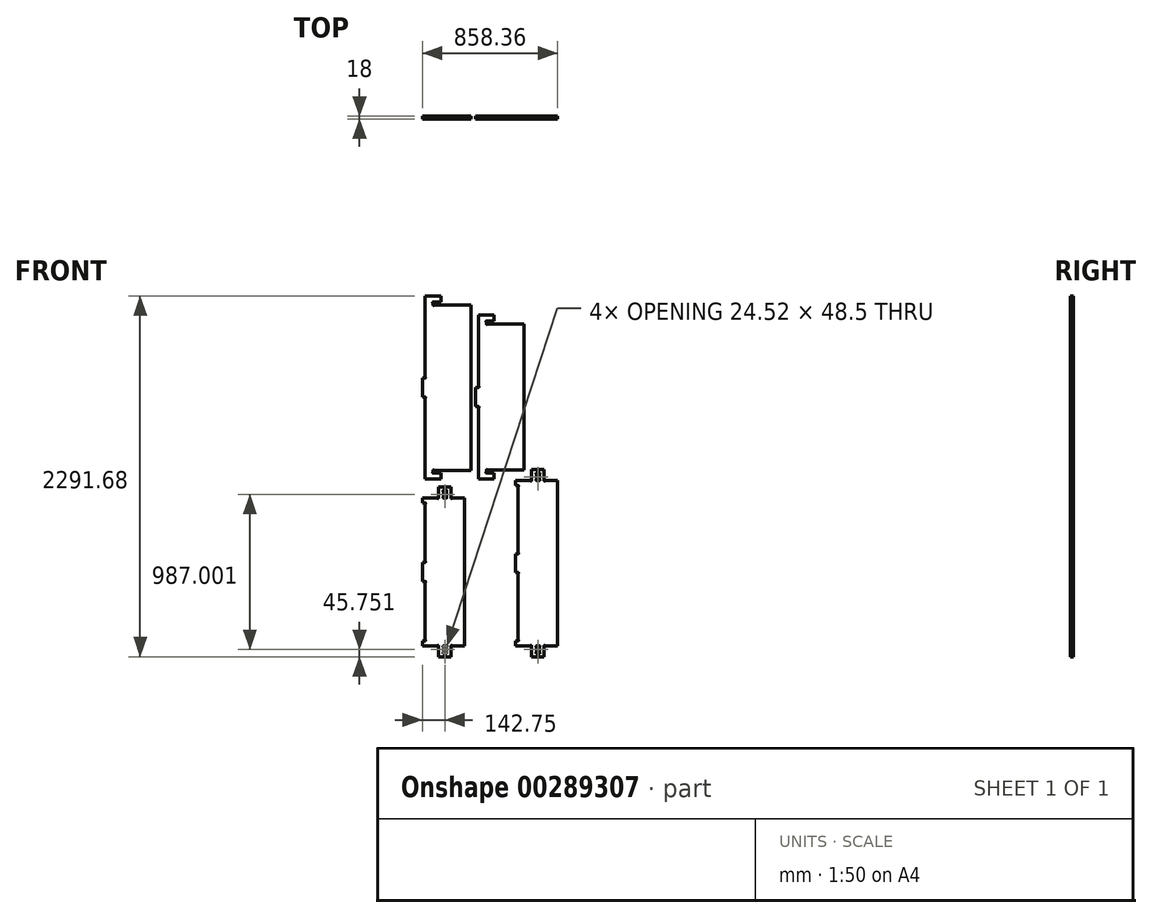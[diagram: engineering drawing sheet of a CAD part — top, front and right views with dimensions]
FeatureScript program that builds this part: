
annotation { "Feature Type Name" : "Feature", "Feature Type Description" : "" }
export const myFeature = defineFeature(function(context is Context, id is Id, definition is map)
    precondition{}
    {
        {
            var Q0;
            Q0=qCreatedBy(makeId("Front.planeOp"),FACE);
            var sketch = newSketch(context, id + "F0", { "sketchPlane" : qUnion([Q0])});
            skLineSegment(sketch, "E0", {"start": v(-600, -1200) * mm, "end": v(600, -1200) * mm});
            skLineSegment(sketch, "E1", {"start": v(600, -1200) * mm, "end": v(600, 1200) * mm});
            skLineSegment(sketch, "E2", {"start": v(600, 1200) * mm, "end": v(-600, 1200) * mm});
            skLineSegment(sketch, "E3", {"start": v(-600, 1200) * mm, "end": v(-600, -1200) * mm});
            skLineSegment(sketch, "E4", {"start": v(-266.04, 1059.68) * mm, "end": v(-501.48, 1059.68) * mm});
            skArc(sketch, "E5", {"start": v(-501.48, 1059.68) * mm, "mid": v(-504.49, 1056.67) * mm, "end": v(-507.5, 1059.68) * mm});
            skLineSegment(sketch, "E6", {"start": v(-507.5, 1059.68) * mm, "end": v(-507.5, 1072.16) * mm});
            skArc(sketch, "E7", {"start": v(-507.5, 1072.16) * mm, "mid": v(-510.5, 1075.17) * mm, "end": v(-507.5, 1078.18) * mm});
            skLineSegment(sketch, "E8", {"start": v(-507.5, 1078.18) * mm, "end": v(-457.5, 1078.18) * mm});
            skLineSegment(sketch, "E9", {"start": v(-457.5, 1078.18) * mm, "end": v(-457.5, 1116.68) * mm});
            skLineSegment(sketch, "E10", {"start": v(-457.5, 1116.68) * mm, "end": v(-557, 1116.68) * mm});
            skLineSegment(sketch, "E11", {"start": v(-557, 1116.68) * mm, "end": v(-557, 600.7) * mm});
            skArc(sketch, "E12", {"start": v(-557, 600.7) * mm, "mid": v(-553.99, 597.69) * mm, "end": v(-557, 594.68) * mm});
            skLineSegment(sketch, "E13", {"start": v(-557, 594.68) * mm, "end": v(-575, 594.68) * mm});
            skLineSegment(sketch, "E14", {"start": v(-575, 594.68) * mm, "end": v(-575, 475.18) * mm});
            skLineSegment(sketch, "E15", {"start": v(-575, 475.18) * mm, "end": v(-557, 475.18) * mm});
            skArc(sketch, "E16", {"start": v(-557, 475.18) * mm, "mid": v(-553.99, 472.17) * mm, "end": v(-557, 469.16) * mm});
            skLineSegment(sketch, "E17", {"start": v(-557, 469.16) * mm, "end": v(-557, -46.82) * mm});
            skLineSegment(sketch, "E18", {"start": v(-557, -46.82) * mm, "end": v(-457.5, -46.82) * mm});
            skLineSegment(sketch, "E19", {"start": v(-457.5, -46.82) * mm, "end": v(-457.5, -8.32) * mm});
            skLineSegment(sketch, "E20", {"start": v(-457.5, -8.32) * mm, "end": v(-507.5, -8.32) * mm});
            skArc(sketch, "E21", {"start": v(-507.5, -8.32) * mm, "mid": v(-510.5, -5.31) * mm, "end": v(-507.5, -2.3) * mm});
            skLineSegment(sketch, "E22", {"start": v(-507.5, -2.3) * mm, "end": v(-507.5, 10.18) * mm});
            skArc(sketch, "E23", {"start": v(-507.5, 10.18) * mm, "mid": v(-504.49, 13.19) * mm, "end": v(-501.48, 10.18) * mm});
            skLineSegment(sketch, "E24", {"start": v(-501.48, 10.18) * mm, "end": v(-266.04, 10.18) * mm});
            skLineSegment(sketch, "E25", {"start": v(-266.04, 10.18) * mm, "end": v(-266.04, 1059.68) * mm});
            skLineSegment(sketch, "E26", {"start": v(-168.7, -1.99) * mm, "end": v(-168.7, 10.5) * mm});
            skArc(sketch, "E27", {"start": v(-168.7, 10.5) * mm, "mid": v(-165.7, 13.5) * mm, "end": v(-162.68, 10.5) * mm});
            skLineSegment(sketch, "E28", {"start": v(-162.68, 10.5) * mm, "end": v(69.97, 10.5) * mm});
            skLineSegment(sketch, "E29", {"start": v(69.97, 10.5) * mm, "end": v(69.97, 940) * mm});
            skLineSegment(sketch, "E30", {"start": v(69.97, 940) * mm, "end": v(-162.68, 940) * mm});
            skArc(sketch, "E31", {"start": v(-162.68, 940) * mm, "mid": v(-165.7, 936.98) * mm, "end": v(-168.7, 940) * mm});
            skLineSegment(sketch, "E32", {"start": v(-168.7, 940) * mm, "end": v(-168.7, 952.47) * mm});
            skArc(sketch, "E33", {"start": v(-168.7, 952.47) * mm, "mid": v(-171.71, 955.48) * mm, "end": v(-168.7, 958.5) * mm});
            skLineSegment(sketch, "E34", {"start": v(-168.7, 958.5) * mm, "end": v(-118.7, 958.5) * mm});
            skLineSegment(sketch, "E35", {"start": v(-118.7, 958.5) * mm, "end": v(-118.7, 997) * mm});
            skLineSegment(sketch, "E36", {"start": v(-118.7, 997) * mm, "end": v(-218.2, 997) * mm});
            skLineSegment(sketch, "E37", {"start": v(-218.2, 997) * mm, "end": v(-218.2, 541.01) * mm});
            skArc(sketch, "E38", {"start": v(-218.2, 541.01) * mm, "mid": v(-215.2, 538) * mm, "end": v(-218.2, 535) * mm});
            skLineSegment(sketch, "E39", {"start": v(-218.2, 535) * mm, "end": v(-236.2, 535) * mm});
            skLineSegment(sketch, "E40", {"start": v(-236.2, 535) * mm, "end": v(-236.2, 415.5) * mm});
            skLineSegment(sketch, "E41", {"start": v(-236.2, 415.5) * mm, "end": v(-218.2, 415.5) * mm});
            skArc(sketch, "E42", {"start": v(-218.2, 415.5) * mm, "mid": v(-215.2, 412.48) * mm, "end": v(-218.2, 409.47) * mm});
            skLineSegment(sketch, "E43", {"start": v(-218.2, 409.47) * mm, "end": v(-218.2, -46.5) * mm});
            skLineSegment(sketch, "E44", {"start": v(-218.2, -46.5) * mm, "end": v(-118.7, -46.5) * mm});
            skLineSegment(sketch, "E45", {"start": v(-118.7, -46.5) * mm, "end": v(-118.7, -8) * mm});
            skLineSegment(sketch, "E46", {"start": v(-118.7, -8) * mm, "end": v(-168.7, -8) * mm});
            skArc(sketch, "E47", {"start": v(-168.7, -8) * mm, "mid": v(-171.71, -5) * mm, "end": v(-168.7, -1.99) * mm});
            skLineSegment(sketch, "E48", {"start": v(575, -55.5) * mm, "end": v(496.02, -55.5) * mm});
            skArc(sketch, "E49", {"start": v(496.02, -55.5) * mm, "mid": v(493, -58.5) * mm, "end": v(490, -55.5) * mm});
            skLineSegment(sketch, "E50", {"start": v(490, -55.5) * mm, "end": v(490, 14.5) * mm});
            skLineSegment(sketch, "E51", {"start": v(490, 14.5) * mm, "end": v(410.5, 14.5) * mm});
            skLineSegment(sketch, "E52", {"start": v(410.5, 14.5) * mm, "end": v(410.5, -55.5) * mm});
            skArc(sketch, "E53", {"start": v(410.5, -55.5) * mm, "mid": v(407.49, -58.5) * mm, "end": v(404.48, -55.5) * mm});
            skLineSegment(sketch, "E54", {"start": v(404.48, -55.5) * mm, "end": v(307.5, -55.5) * mm});
            skLineSegment(sketch, "E55", {"start": v(307.5, -55.5) * mm, "end": v(307.5, -86) * mm});
            skLineSegment(sketch, "E56", {"start": v(307.5, -86) * mm, "end": v(325.5, -86) * mm});
            skArc(sketch, "E57", {"start": v(325.5, -86) * mm, "mid": v(328.5, -89) * mm, "end": v(325.5, -92.02) * mm});
            skLineSegment(sketch, "E58", {"start": v(325.5, -92.02) * mm, "end": v(325.5, -514.48) * mm});
            skArc(sketch, "E59", {"start": v(325.5, -514.48) * mm, "mid": v(328.5, -517.49) * mm, "end": v(325.5, -520.5) * mm});
            skLineSegment(sketch, "E60", {"start": v(325.5, -520.5) * mm, "end": v(307.5, -520.5) * mm});
            skLineSegment(sketch, "E61", {"start": v(307.5, -520.5) * mm, "end": v(307.5, -640) * mm});
            skLineSegment(sketch, "E62", {"start": v(307.5, -640) * mm, "end": v(325.5, -640) * mm});
            skArc(sketch, "E63", {"start": v(325.5, -640) * mm, "mid": v(328.5, -643) * mm, "end": v(325.5, -646.02) * mm});
            skLineSegment(sketch, "E64", {"start": v(325.5, -646.02) * mm, "end": v(325.5, -1068.48) * mm});
            skArc(sketch, "E65", {"start": v(325.5, -1068.48) * mm, "mid": v(328.5, -1071.49) * mm, "end": v(325.5, -1074.5) * mm});
            skLineSegment(sketch, "E66", {"start": v(325.5, -1074.5) * mm, "end": v(307.5, -1074.5) * mm});
            skLineSegment(sketch, "E67", {"start": v(307.5, -1074.5) * mm, "end": v(307.5, -1105) * mm});
            skLineSegment(sketch, "E68", {"start": v(307.5, -1105) * mm, "end": v(404.48, -1105) * mm});
            skArc(sketch, "E69", {"start": v(404.48, -1105) * mm, "mid": v(407.49, -1101.99) * mm, "end": v(410.5, -1105) * mm});
            skLineSegment(sketch, "E70", {"start": v(410.5, -1105) * mm, "end": v(410.5, -1175) * mm});
            skLineSegment(sketch, "E71", {"start": v(410.5, -1175) * mm, "end": v(490, -1175) * mm});
            skLineSegment(sketch, "E72", {"start": v(490, -1175) * mm, "end": v(490, -1105) * mm});
            skArc(sketch, "E73", {"start": v(490, -1105) * mm, "mid": v(493, -1101.99) * mm, "end": v(496.02, -1105) * mm});
            skLineSegment(sketch, "E74", {"start": v(496.02, -1105) * mm, "end": v(575, -1105) * mm});
            skLineSegment(sketch, "E75", {"start": v(575, -1105) * mm, "end": v(575, -55.5) * mm});
            skLineSegment(sketch, "E76", {"start": v(-15.96, -166.5) * mm, "end": v(-94.94, -166.5) * mm});
            skArc(sketch, "E77", {"start": v(-94.94, -166.5) * mm, "mid": v(-97.95, -169.5) * mm, "end": v(-100.96, -166.5) * mm});
            skLineSegment(sketch, "E78", {"start": v(-100.96, -166.5) * mm, "end": v(-100.96, -96.5) * mm});
            skLineSegment(sketch, "E79", {"start": v(-100.96, -96.5) * mm, "end": v(-180.46, -96.5) * mm});
            skLineSegment(sketch, "E80", {"start": v(-180.46, -96.5) * mm, "end": v(-180.46, -166.5) * mm});
            skArc(sketch, "E81", {"start": v(-180.46, -166.5) * mm, "mid": v(-183.47, -169.5) * mm, "end": v(-186.48, -166.5) * mm});
            skLineSegment(sketch, "E82", {"start": v(-186.48, -166.5) * mm, "end": v(-283.46, -166.5) * mm});
            skLineSegment(sketch, "E83", {"start": v(-283.46, -166.5) * mm, "end": v(-283.46, -197) * mm});
            skLineSegment(sketch, "E84", {"start": v(-283.46, -197) * mm, "end": v(-265.46, -197) * mm});
            skArc(sketch, "E85", {"start": v(-265.46, -197) * mm, "mid": v(-262.45, -200) * mm, "end": v(-265.46, -203.02) * mm});
            skLineSegment(sketch, "E86", {"start": v(-265.46, -203.02) * mm, "end": v(-265.46, -569.98) * mm});
            skArc(sketch, "E87", {"start": v(-265.46, -569.98) * mm, "mid": v(-262.45, -572.99) * mm, "end": v(-265.46, -576) * mm});
            skLineSegment(sketch, "E88", {"start": v(-265.46, -576) * mm, "end": v(-283.46, -576) * mm});
            skLineSegment(sketch, "E89", {"start": v(-283.46, -576) * mm, "end": v(-283.46, -695.5) * mm});
            skLineSegment(sketch, "E90", {"start": v(-283.46, -695.5) * mm, "end": v(-265.46, -695.5) * mm});
            skArc(sketch, "E91", {"start": v(-265.46, -695.5) * mm, "mid": v(-262.45, -698.5) * mm, "end": v(-265.46, -701.52) * mm});
            skLineSegment(sketch, "E92", {"start": v(-265.46, -701.52) * mm, "end": v(-265.46, -1068.48) * mm});
            skArc(sketch, "E93", {"start": v(-265.46, -1068.48) * mm, "mid": v(-262.45, -1071.49) * mm, "end": v(-265.46, -1074.5) * mm});
            skLineSegment(sketch, "E94", {"start": v(-265.46, -1074.5) * mm, "end": v(-283.46, -1074.5) * mm});
            skLineSegment(sketch, "E95", {"start": v(-283.46, -1074.5) * mm, "end": v(-283.46, -1105) * mm});
            skLineSegment(sketch, "E96", {"start": v(-283.46, -1105) * mm, "end": v(-186.48, -1105) * mm});
            skArc(sketch, "E97", {"start": v(-186.48, -1105) * mm, "mid": v(-183.47, -1101.99) * mm, "end": v(-180.46, -1105) * mm});
            skLineSegment(sketch, "E98", {"start": v(-180.46, -1105) * mm, "end": v(-180.46, -1175) * mm});
            skLineSegment(sketch, "E99", {"start": v(-180.46, -1175) * mm, "end": v(-100.96, -1175) * mm});
            skLineSegment(sketch, "E100", {"start": v(-100.96, -1175) * mm, "end": v(-100.96, -1105) * mm});
            skArc(sketch, "E101", {"start": v(-100.96, -1105) * mm, "mid": v(-97.95, -1101.99) * mm, "end": v(-94.94, -1105) * mm});
            skLineSegment(sketch, "E102", {"start": v(-94.94, -1105) * mm, "end": v(-15.96, -1105) * mm});
            skLineSegment(sketch, "E103", {"start": v(-15.96, -1105) * mm, "end": v(-15.96, -166.5) * mm});
            skLineSegment(sketch, "E104", {"start": v(-307.5, -166.5) * mm, "end": v(-386.48, -166.5) * mm});
            skArc(sketch, "E105", {"start": v(-386.48, -166.5) * mm, "mid": v(-389.49, -169.5) * mm, "end": v(-392.5, -166.5) * mm});
            skLineSegment(sketch, "E106", {"start": v(-392.5, -166.5) * mm, "end": v(-392.5, -96.5) * mm});
            skLineSegment(sketch, "E107", {"start": v(-392.5, -96.5) * mm, "end": v(-472, -96.5) * mm});
            skLineSegment(sketch, "E108", {"start": v(-472, -96.5) * mm, "end": v(-472, -166.5) * mm});
            skArc(sketch, "E109", {"start": v(-472, -166.5) * mm, "mid": v(-475, -169.5) * mm, "end": v(-478.02, -166.5) * mm});
            skLineSegment(sketch, "E110", {"start": v(-478.02, -166.5) * mm, "end": v(-575, -166.5) * mm});
            skLineSegment(sketch, "E111", {"start": v(-575, -166.5) * mm, "end": v(-575, -197) * mm});
            skLineSegment(sketch, "E112", {"start": v(-575, -197) * mm, "end": v(-557, -197) * mm});
            skArc(sketch, "E113", {"start": v(-557, -197) * mm, "mid": v(-553.99, -200) * mm, "end": v(-557, -203.02) * mm});
            skLineSegment(sketch, "E114", {"start": v(-557, -203.02) * mm, "end": v(-557, -569.98) * mm});
            skArc(sketch, "E115", {"start": v(-557, -569.98) * mm, "mid": v(-553.99, -572.99) * mm, "end": v(-557, -576) * mm});
            skLineSegment(sketch, "E116", {"start": v(-557, -576) * mm, "end": v(-575, -576) * mm});
            skLineSegment(sketch, "E117", {"start": v(-575, -576) * mm, "end": v(-575, -695.5) * mm});
            skLineSegment(sketch, "E118", {"start": v(-575, -695.5) * mm, "end": v(-557, -695.5) * mm});
            skArc(sketch, "E119", {"start": v(-557, -695.5) * mm, "mid": v(-553.99, -698.5) * mm, "end": v(-557, -701.52) * mm});
            skLineSegment(sketch, "E120", {"start": v(-557, -701.52) * mm, "end": v(-557, -1068.48) * mm});
            skArc(sketch, "E121", {"start": v(-557, -1068.48) * mm, "mid": v(-553.99, -1071.49) * mm, "end": v(-557, -1074.5) * mm});
            skLineSegment(sketch, "E122", {"start": v(-557, -1074.5) * mm, "end": v(-575, -1074.5) * mm});
            skLineSegment(sketch, "E123", {"start": v(-575, -1074.5) * mm, "end": v(-575, -1105) * mm});
            skLineSegment(sketch, "E124", {"start": v(-575, -1105) * mm, "end": v(-478.02, -1105) * mm});
            skArc(sketch, "E125", {"start": v(-478.02, -1105) * mm, "mid": v(-475, -1101.99) * mm, "end": v(-472, -1105) * mm});
            skLineSegment(sketch, "E126", {"start": v(-472, -1105) * mm, "end": v(-472, -1175) * mm});
            skLineSegment(sketch, "E127", {"start": v(-472, -1175) * mm, "end": v(-392.5, -1175) * mm});
            skLineSegment(sketch, "E128", {"start": v(-392.5, -1175) * mm, "end": v(-392.5, -1105) * mm});
            skArc(sketch, "E129", {"start": v(-392.5, -1105) * mm, "mid": v(-389.49, -1101.99) * mm, "end": v(-386.48, -1105) * mm});
            skLineSegment(sketch, "E130", {"start": v(-386.48, -1105) * mm, "end": v(-307.5, -1105) * mm});
            skLineSegment(sketch, "E131", {"start": v(-307.5, -1105) * mm, "end": v(-307.5, -166.5) * mm});
            skLineSegment(sketch, "E132", {"start": v(283.36, -55.5) * mm, "end": v(204.38, -55.5) * mm});
            skArc(sketch, "E133", {"start": v(204.38, -55.5) * mm, "mid": v(201.37, -58.5) * mm, "end": v(198.36, -55.5) * mm});
            skLineSegment(sketch, "E134", {"start": v(198.36, -55.5) * mm, "end": v(198.36, 14.5) * mm});
            skLineSegment(sketch, "E135", {"start": v(198.36, 14.5) * mm, "end": v(118.86, 14.5) * mm});
            skLineSegment(sketch, "E136", {"start": v(118.86, 14.5) * mm, "end": v(118.86, -55.5) * mm});
            skArc(sketch, "E137", {"start": v(118.86, -55.5) * mm, "mid": v(115.85, -58.5) * mm, "end": v(112.84, -55.5) * mm});
            skLineSegment(sketch, "E138", {"start": v(112.84, -55.5) * mm, "end": v(15.86, -55.5) * mm});
            skLineSegment(sketch, "E139", {"start": v(15.86, -55.5) * mm, "end": v(15.86, -86) * mm});
            skLineSegment(sketch, "E140", {"start": v(15.86, -86) * mm, "end": v(33.86, -86) * mm});
            skArc(sketch, "E141", {"start": v(33.86, -86) * mm, "mid": v(36.87, -89) * mm, "end": v(33.86, -92.02) * mm});
            skLineSegment(sketch, "E142", {"start": v(33.86, -92.02) * mm, "end": v(33.86, -514.48) * mm});
            skArc(sketch, "E143", {"start": v(33.86, -514.48) * mm, "mid": v(36.87, -517.49) * mm, "end": v(33.86, -520.5) * mm});
            skLineSegment(sketch, "E144", {"start": v(33.86, -520.5) * mm, "end": v(15.86, -520.5) * mm});
            skLineSegment(sketch, "E145", {"start": v(15.86, -520.5) * mm, "end": v(15.86, -640) * mm});
            skLineSegment(sketch, "E146", {"start": v(15.86, -640) * mm, "end": v(33.86, -640) * mm});
            skArc(sketch, "E147", {"start": v(33.86, -640) * mm, "mid": v(36.87, -643) * mm, "end": v(33.86, -646.02) * mm});
            skLineSegment(sketch, "E148", {"start": v(33.86, -646.02) * mm, "end": v(33.86, -1068.48) * mm});
            skArc(sketch, "E149", {"start": v(33.86, -1068.48) * mm, "mid": v(36.87, -1071.49) * mm, "end": v(33.86, -1074.5) * mm});
            skLineSegment(sketch, "E150", {"start": v(33.86, -1074.5) * mm, "end": v(15.86, -1074.5) * mm});
            skLineSegment(sketch, "E151", {"start": v(15.86, -1074.5) * mm, "end": v(15.86, -1105) * mm});
            skLineSegment(sketch, "E152", {"start": v(15.86, -1105) * mm, "end": v(112.84, -1105) * mm});
            skArc(sketch, "E153", {"start": v(112.84, -1105) * mm, "mid": v(115.85, -1101.99) * mm, "end": v(118.86, -1105) * mm});
            skLineSegment(sketch, "E154", {"start": v(118.86, -1105) * mm, "end": v(118.86, -1175) * mm});
            skLineSegment(sketch, "E155", {"start": v(118.86, -1175) * mm, "end": v(198.36, -1175) * mm});
            skLineSegment(sketch, "E156", {"start": v(198.36, -1175) * mm, "end": v(198.36, -1105) * mm});
            skArc(sketch, "E157", {"start": v(198.36, -1105) * mm, "mid": v(201.37, -1101.99) * mm, "end": v(204.38, -1105) * mm});
            skLineSegment(sketch, "E158", {"start": v(204.38, -1105) * mm, "end": v(283.36, -1105) * mm});
            skLineSegment(sketch, "E159", {"start": v(283.36, -1105) * mm, "end": v(283.36, -55.5) * mm});
            skLineSegment(sketch, "E160", {"start": v(459.5, -1147.48) * mm, "end": v(459.5, -1111.02) * mm});
            skArc(sketch, "E161", {"start": v(459.5, -1111.02) * mm, "mid": v(462.5, -1108) * mm, "end": v(459.5, -1105) * mm});
            skLineSegment(sketch, "E162", {"start": v(459.5, -1105) * mm, "end": v(441, -1105) * mm});
            skArc(sketch, "E163", {"start": v(441, -1105) * mm, "mid": v(437.99, -1108) * mm, "end": v(441, -1111.02) * mm});
            skLineSegment(sketch, "E164", {"start": v(441, -1111.02) * mm, "end": v(441, -1147.48) * mm});
            skArc(sketch, "E165", {"start": v(441, -1147.48) * mm, "mid": v(437.99, -1150.49) * mm, "end": v(441, -1153.5) * mm});
            skLineSegment(sketch, "E166", {"start": v(441, -1153.5) * mm, "end": v(459.5, -1153.5) * mm});
            skArc(sketch, "E167", {"start": v(459.5, -1153.5) * mm, "mid": v(462.5, -1150.49) * mm, "end": v(459.5, -1147.48) * mm});
            skLineSegment(sketch, "E168", {"start": v(459.5, -49.48) * mm, "end": v(459.5, -13.02) * mm});
            skArc(sketch, "E169", {"start": v(459.5, -13.02) * mm, "mid": v(462.5, -10) * mm, "end": v(459.5, -7) * mm});
            skLineSegment(sketch, "E170", {"start": v(459.5, -7) * mm, "end": v(441, -7) * mm});
            skArc(sketch, "E171", {"start": v(441, -7) * mm, "mid": v(437.99, -10) * mm, "end": v(441, -13.02) * mm});
            skLineSegment(sketch, "E172", {"start": v(441, -13.02) * mm, "end": v(441, -49.48) * mm});
            skArc(sketch, "E173", {"start": v(441, -49.48) * mm, "mid": v(437.99, -52.49) * mm, "end": v(441, -55.5) * mm});
            skLineSegment(sketch, "E174", {"start": v(441, -55.5) * mm, "end": v(459.5, -55.5) * mm});
            skArc(sketch, "E175", {"start": v(459.5, -55.5) * mm, "mid": v(462.5, -52.49) * mm, "end": v(459.5, -49.48) * mm});
            skLineSegment(sketch, "E176", {"start": v(-131.46, -1147.48) * mm, "end": v(-131.46, -1111.02) * mm});
            skArc(sketch, "E177", {"start": v(-131.46, -1111.02) * mm, "mid": v(-128.45, -1108) * mm, "end": v(-131.46, -1105) * mm});
            skLineSegment(sketch, "E178", {"start": v(-131.46, -1105) * mm, "end": v(-149.96, -1105) * mm});
            skArc(sketch, "E179", {"start": v(-149.96, -1105) * mm, "mid": v(-152.97, -1108) * mm, "end": v(-149.96, -1111.02) * mm});
            skLineSegment(sketch, "E180", {"start": v(-149.96, -1111.02) * mm, "end": v(-149.96, -1147.48) * mm});
            skArc(sketch, "E181", {"start": v(-149.96, -1147.48) * mm, "mid": v(-152.97, -1150.49) * mm, "end": v(-149.96, -1153.5) * mm});
            skLineSegment(sketch, "E182", {"start": v(-149.96, -1153.5) * mm, "end": v(-131.46, -1153.5) * mm});
            skArc(sketch, "E183", {"start": v(-131.46, -1153.5) * mm, "mid": v(-128.45, -1150.49) * mm, "end": v(-131.46, -1147.48) * mm});
            skLineSegment(sketch, "E184", {"start": v(-149.96, -124.02) * mm, "end": v(-149.96, -160.48) * mm});
            skArc(sketch, "E185", {"start": v(-149.96, -160.48) * mm, "mid": v(-152.97, -163.49) * mm, "end": v(-149.96, -166.5) * mm});
            skLineSegment(sketch, "E186", {"start": v(-149.96, -166.5) * mm, "end": v(-131.46, -166.5) * mm});
            skArc(sketch, "E187", {"start": v(-131.46, -166.5) * mm, "mid": v(-128.45, -163.49) * mm, "end": v(-131.46, -160.48) * mm});
            skLineSegment(sketch, "E188", {"start": v(-131.46, -160.48) * mm, "end": v(-131.46, -124.02) * mm});
            skArc(sketch, "E189", {"start": v(-131.46, -124.02) * mm, "mid": v(-128.45, -121) * mm, "end": v(-131.46, -118) * mm});
            skLineSegment(sketch, "E190", {"start": v(-131.46, -118) * mm, "end": v(-149.96, -118) * mm});
            skArc(sketch, "E191", {"start": v(-149.96, -118) * mm, "mid": v(-152.97, -121) * mm, "end": v(-149.96, -124.02) * mm});
            skLineSegment(sketch, "E192", {"start": v(-423, -1147.48) * mm, "end": v(-423, -1111.02) * mm});
            skArc(sketch, "E193", {"start": v(-423, -1111.02) * mm, "mid": v(-419.99, -1108) * mm, "end": v(-423, -1105) * mm});
            skLineSegment(sketch, "E194", {"start": v(-423, -1105) * mm, "end": v(-441.5, -1105) * mm});
            skArc(sketch, "E195", {"start": v(-441.5, -1105) * mm, "mid": v(-444.5, -1108) * mm, "end": v(-441.5, -1111.02) * mm});
            skLineSegment(sketch, "E196", {"start": v(-441.5, -1111.02) * mm, "end": v(-441.5, -1147.48) * mm});
            skArc(sketch, "E197", {"start": v(-441.5, -1147.48) * mm, "mid": v(-444.5, -1150.49) * mm, "end": v(-441.5, -1153.5) * mm});
            skLineSegment(sketch, "E198", {"start": v(-441.5, -1153.5) * mm, "end": v(-423, -1153.5) * mm});
            skArc(sketch, "E199", {"start": v(-423, -1153.5) * mm, "mid": v(-419.99, -1150.49) * mm, "end": v(-423, -1147.48) * mm});
            skLineSegment(sketch, "E200", {"start": v(-441.5, -124.02) * mm, "end": v(-441.5, -160.48) * mm});
            skArc(sketch, "E201", {"start": v(-441.5, -160.48) * mm, "mid": v(-444.5, -163.49) * mm, "end": v(-441.5, -166.5) * mm});
            skLineSegment(sketch, "E202", {"start": v(-441.5, -166.5) * mm, "end": v(-423, -166.5) * mm});
            skArc(sketch, "E203", {"start": v(-423, -166.5) * mm, "mid": v(-419.99, -163.49) * mm, "end": v(-423, -160.48) * mm});
            skLineSegment(sketch, "E204", {"start": v(-423, -160.48) * mm, "end": v(-423, -124.02) * mm});
            skArc(sketch, "E205", {"start": v(-423, -124.02) * mm, "mid": v(-419.99, -121) * mm, "end": v(-423, -118) * mm});
            skLineSegment(sketch, "E206", {"start": v(-423, -118) * mm, "end": v(-441.5, -118) * mm});
            skArc(sketch, "E207", {"start": v(-441.5, -118) * mm, "mid": v(-444.5, -121) * mm, "end": v(-441.5, -124.02) * mm});
            skLineSegment(sketch, "E208", {"start": v(167.86, -1147.48) * mm, "end": v(167.86, -1111.02) * mm});
            skArc(sketch, "E209", {"start": v(167.86, -1111.02) * mm, "mid": v(170.87, -1108) * mm, "end": v(167.86, -1105) * mm});
            skLineSegment(sketch, "E210", {"start": v(167.86, -1105) * mm, "end": v(149.36, -1105) * mm});
            skArc(sketch, "E211", {"start": v(149.36, -1105) * mm, "mid": v(146.35, -1108) * mm, "end": v(149.36, -1111.02) * mm});
            skLineSegment(sketch, "E212", {"start": v(149.36, -1111.02) * mm, "end": v(149.36, -1147.48) * mm});
            skArc(sketch, "E213", {"start": v(149.36, -1147.48) * mm, "mid": v(146.35, -1150.49) * mm, "end": v(149.36, -1153.5) * mm});
            skLineSegment(sketch, "E214", {"start": v(149.36, -1153.5) * mm, "end": v(167.86, -1153.5) * mm});
            skArc(sketch, "E215", {"start": v(167.86, -1153.5) * mm, "mid": v(170.87, -1150.49) * mm, "end": v(167.86, -1147.48) * mm});
            skLineSegment(sketch, "E216", {"start": v(167.86, -49.48) * mm, "end": v(167.86, -13.02) * mm});
            skArc(sketch, "E217", {"start": v(167.86, -13.02) * mm, "mid": v(170.87, -10) * mm, "end": v(167.86, -7) * mm});
            skLineSegment(sketch, "E218", {"start": v(167.86, -7) * mm, "end": v(149.36, -7) * mm});
            skArc(sketch, "E219", {"start": v(149.36, -7) * mm, "mid": v(146.35, -10) * mm, "end": v(149.36, -13.02) * mm});
            skLineSegment(sketch, "E220", {"start": v(149.36, -13.02) * mm, "end": v(149.36, -49.48) * mm});
            skArc(sketch, "E221", {"start": v(149.36, -49.48) * mm, "mid": v(146.35, -52.49) * mm, "end": v(149.36, -55.5) * mm});
            skLineSegment(sketch, "E222", {"start": v(149.36, -55.5) * mm, "end": v(167.86, -55.5) * mm});
            skArc(sketch, "E223", {"start": v(167.86, -55.5) * mm, "mid": v(170.87, -52.49) * mm, "end": v(167.86, -49.48) * mm});
            skArc(sketch, "E224", {"start": v(-568.7, -1170.76) * mm, "mid": v(-570.83, -1171.64) * mm, "end": v(-571.7, -1173.76) * mm});
            skArc(sketch, "E225", {"start": v(-571.7, -1173.76) * mm, "mid": v(-570.83, -1175.88) * mm, "end": v(-568.7, -1176.76) * mm});
            skArc(sketch, "E226", {"start": v(-568.7, -1176.76) * mm, "mid": v(-566.59, -1175.88) * mm, "end": v(-565.7, -1173.76) * mm});
            skArc(sketch, "E227", {"start": v(-565.7, -1173.76) * mm, "mid": v(-566.59, -1171.64) * mm, "end": v(-568.7, -1170.76) * mm});
            skArc(sketch, "E228", {"start": v(565.94, -1165.92) * mm, "mid": v(563.82, -1166.8) * mm, "end": v(562.94, -1168.92) * mm});
            skArc(sketch, "E229", {"start": v(562.94, -1168.92) * mm, "mid": v(563.82, -1171.04) * mm, "end": v(565.94, -1171.92) * mm});
            skArc(sketch, "E230", {"start": v(565.94, -1171.92) * mm, "mid": v(568.06, -1171.04) * mm, "end": v(568.94, -1168.92) * mm});
            skArc(sketch, "E231", {"start": v(568.94, -1168.92) * mm, "mid": v(568.06, -1166.8) * mm, "end": v(565.94, -1165.92) * mm});
            skArc(sketch, "E232", {"start": v(229.76, -1165.92) * mm, "mid": v(227.64, -1166.8) * mm, "end": v(226.76, -1168.92) * mm});
            skArc(sketch, "E233", {"start": v(226.76, -1168.92) * mm, "mid": v(227.64, -1171.04) * mm, "end": v(229.76, -1171.92) * mm});
            skArc(sketch, "E234", {"start": v(229.76, -1171.92) * mm, "mid": v(231.88, -1171.04) * mm, "end": v(232.76, -1168.92) * mm});
            skArc(sketch, "E235", {"start": v(232.76, -1168.92) * mm, "mid": v(231.88, -1166.8) * mm, "end": v(229.76, -1165.92) * mm});
            skArc(sketch, "E236", {"start": v(-74.72, -1164.07) * mm, "mid": v(-76.84, -1164.95) * mm, "end": v(-77.72, -1167.07) * mm});
            skArc(sketch, "E237", {"start": v(-77.72, -1167.07) * mm, "mid": v(-76.84, -1169.2) * mm, "end": v(-74.72, -1170.07) * mm});
            skArc(sketch, "E238", {"start": v(-74.72, -1170.07) * mm, "mid": v(-72.6, -1169.2) * mm, "end": v(-71.72, -1167.07) * mm});
            skArc(sketch, "E239", {"start": v(-71.72, -1167.07) * mm, "mid": v(-72.6, -1164.95) * mm, "end": v(-74.72, -1164.07) * mm});
            skArc(sketch, "E240", {"start": v(-578.64, -721.42) * mm, "mid": v(-580.77, -722.3) * mm, "end": v(-581.64, -724.42) * mm});
            skArc(sketch, "E241", {"start": v(-581.64, -724.42) * mm, "mid": v(-580.77, -726.54) * mm, "end": v(-578.64, -727.42) * mm});
            skArc(sketch, "E242", {"start": v(-578.64, -727.42) * mm, "mid": v(-576.52, -726.54) * mm, "end": v(-575.64, -724.42) * mm});
            skArc(sketch, "E243", {"start": v(-575.64, -724.42) * mm, "mid": v(-576.52, -722.3) * mm, "end": v(-578.64, -721.42) * mm});
            skArc(sketch, "E244", {"start": v(-286.18, -540.3) * mm, "mid": v(-288.3, -541.17) * mm, "end": v(-289.18, -543.3) * mm});
            skArc(sketch, "E245", {"start": v(-289.18, -543.3) * mm, "mid": v(-288.3, -545.41) * mm, "end": v(-286.18, -546.3) * mm});
            skArc(sketch, "E246", {"start": v(-286.18, -546.3) * mm, "mid": v(-284.06, -545.41) * mm, "end": v(-283.18, -543.3) * mm});
            skArc(sketch, "E247", {"start": v(-283.18, -543.3) * mm, "mid": v(-284.06, -541.17) * mm, "end": v(-286.18, -540.3) * mm});
            skArc(sketch, "E248", {"start": v(7.89, -672.55) * mm, "mid": v(5.77, -673.43) * mm, "end": v(4.89, -675.55) * mm});
            skArc(sketch, "E249", {"start": v(4.89, -675.55) * mm, "mid": v(5.77, -677.67) * mm, "end": v(7.89, -678.55) * mm});
            skArc(sketch, "E250", {"start": v(7.89, -678.55) * mm, "mid": v(10, -677.67) * mm, "end": v(10.89, -675.55) * mm});
            skArc(sketch, "E251", {"start": v(10.89, -675.55) * mm, "mid": v(10, -673.43) * mm, "end": v(7.89, -672.55) * mm});
            skArc(sketch, "E252", {"start": v(305.54, -483.46) * mm, "mid": v(303.42, -484.34) * mm, "end": v(302.54, -486.46) * mm});
            skArc(sketch, "E253", {"start": v(302.54, -486.46) * mm, "mid": v(303.42, -488.58) * mm, "end": v(305.54, -489.46) * mm});
            skArc(sketch, "E254", {"start": v(305.54, -489.46) * mm, "mid": v(307.66, -488.58) * mm, "end": v(308.54, -486.46) * mm});
            skArc(sketch, "E255", {"start": v(308.54, -486.46) * mm, "mid": v(307.66, -484.34) * mm, "end": v(305.54, -483.46) * mm});
            skArc(sketch, "E256", {"start": v(-536.31, -116.84) * mm, "mid": v(-538.43, -117.72) * mm, "end": v(-539.31, -119.84) * mm});
            skArc(sketch, "E257", {"start": v(-539.31, -119.84) * mm, "mid": v(-538.43, -121.96) * mm, "end": v(-536.31, -122.84) * mm});
            skArc(sketch, "E258", {"start": v(-536.31, -122.84) * mm, "mid": v(-534.2, -121.96) * mm, "end": v(-533.31, -119.84) * mm});
            skArc(sketch, "E259", {"start": v(-533.31, -119.84) * mm, "mid": v(-534.2, -117.72) * mm, "end": v(-536.31, -116.84) * mm});
            skArc(sketch, "E260", {"start": v(-60.82, -77.93) * mm, "mid": v(-62.94, -78.8) * mm, "end": v(-63.82, -80.93) * mm});
            skArc(sketch, "E261", {"start": v(-63.82, -80.93) * mm, "mid": v(-62.94, -83.05) * mm, "end": v(-60.82, -83.93) * mm});
            skArc(sketch, "E262", {"start": v(-60.82, -83.93) * mm, "mid": v(-58.7, -83.05) * mm, "end": v(-57.82, -80.93) * mm});
            skArc(sketch, "E263", {"start": v(-57.82, -80.93) * mm, "mid": v(-58.7, -78.8) * mm, "end": v(-60.82, -77.93) * mm});
            skArc(sketch, "E264", {"start": v(338.44, 17.96) * mm, "mid": v(336.32, 17.09) * mm, "end": v(335.44, 14.96) * mm});
            skArc(sketch, "E265", {"start": v(335.44, 14.96) * mm, "mid": v(336.32, 12.84) * mm, "end": v(338.44, 11.96) * mm});
            skArc(sketch, "E266", {"start": v(338.44, 11.96) * mm, "mid": v(340.56, 12.84) * mm, "end": v(341.44, 14.96) * mm});
            skArc(sketch, "E267", {"start": v(341.44, 14.96) * mm, "mid": v(340.56, 17.09) * mm, "end": v(338.44, 17.96) * mm});
            skArc(sketch, "E268", {"start": v(87.67, 406.57) * mm, "mid": v(85.55, 405.69) * mm, "end": v(84.67, 403.57) * mm});
            skArc(sketch, "E269", {"start": v(84.67, 403.57) * mm, "mid": v(85.55, 401.45) * mm, "end": v(87.67, 400.57) * mm});
            skArc(sketch, "E270", {"start": v(87.67, 400.57) * mm, "mid": v(89.8, 401.45) * mm, "end": v(90.67, 403.57) * mm});
            skArc(sketch, "E271", {"start": v(90.67, 403.57) * mm, "mid": v(89.8, 405.69) * mm, "end": v(87.67, 406.57) * mm});
            skArc(sketch, "E272", {"start": v(-240.89, 571.74) * mm, "mid": v(-243, 570.87) * mm, "end": v(-243.89, 568.74) * mm});
            skArc(sketch, "E273", {"start": v(-243.89, 568.74) * mm, "mid": v(-243, 566.62) * mm, "end": v(-240.89, 565.74) * mm});
            skArc(sketch, "E274", {"start": v(-240.89, 565.74) * mm, "mid": v(-238.76, 566.62) * mm, "end": v(-237.89, 568.74) * mm});
            skArc(sketch, "E275", {"start": v(-237.89, 568.74) * mm, "mid": v(-238.76, 570.87) * mm, "end": v(-240.89, 571.74) * mm});
            skArc(sketch, "E276", {"start": v(-578.18, 636.2) * mm, "mid": v(-580.3, 635.33) * mm, "end": v(-581.18, 633.2) * mm});
            skArc(sketch, "E277", {"start": v(-581.18, 633.2) * mm, "mid": v(-580.3, 631.08) * mm, "end": v(-578.18, 630.2) * mm});
            skArc(sketch, "E278", {"start": v(-578.18, 630.2) * mm, "mid": v(-576.06, 631.08) * mm, "end": v(-575.18, 633.2) * mm});
            skArc(sketch, "E279", {"start": v(-575.18, 633.2) * mm, "mid": v(-576.06, 635.33) * mm, "end": v(-578.18, 636.2) * mm});
            skArc(sketch, "E280", {"start": v(-535.95, 1153.78) * mm, "mid": v(-538.08, 1152.9) * mm, "end": v(-538.95, 1150.78) * mm});
            skArc(sketch, "E281", {"start": v(-538.95, 1150.78) * mm, "mid": v(-538.08, 1148.66) * mm, "end": v(-535.95, 1147.78) * mm});
            skArc(sketch, "E282", {"start": v(-535.95, 1147.78) * mm, "mid": v(-533.83, 1148.66) * mm, "end": v(-532.95, 1150.78) * mm});
            skArc(sketch, "E283", {"start": v(-532.95, 1150.78) * mm, "mid": v(-533.83, 1152.9) * mm, "end": v(-535.95, 1153.78) * mm});
            skArc(sketch, "E284", {"start": v(-232.53, 1028.1) * mm, "mid": v(-234.65, 1027.23) * mm, "end": v(-235.53, 1025.1) * mm});
            skArc(sketch, "E285", {"start": v(-235.53, 1025.1) * mm, "mid": v(-234.65, 1022.99) * mm, "end": v(-232.53, 1022.1) * mm});
            skArc(sketch, "E286", {"start": v(-232.53, 1022.1) * mm, "mid": v(-230.41, 1022.99) * mm, "end": v(-229.53, 1025.1) * mm});
            skArc(sketch, "E287", {"start": v(-229.53, 1025.1) * mm, "mid": v(-230.41, 1027.23) * mm, "end": v(-232.53, 1028.1) * mm});
            skArc(sketch, "E288", {"start": v(92.43, 922.18) * mm, "mid": v(90.31, 921.3) * mm, "end": v(89.43, 919.18) * mm});
            skArc(sketch, "E289", {"start": v(89.43, 919.18) * mm, "mid": v(90.31, 917.06) * mm, "end": v(92.43, 916.18) * mm});
            skArc(sketch, "E290", {"start": v(92.43, 916.18) * mm, "mid": v(94.55, 917.06) * mm, "end": v(95.43, 919.18) * mm});
            skArc(sketch, "E291", {"start": v(95.43, 919.18) * mm, "mid": v(94.55, 921.3) * mm, "end": v(92.43, 922.18) * mm});
            skArc(sketch, "E292", {"start": v(577.63, -31.02) * mm, "mid": v(575.5, -31.9) * mm, "end": v(574.63, -34.02) * mm});
            skArc(sketch, "E293", {"start": v(574.63, -34.02) * mm, "mid": v(575.5, -36.14) * mm, "end": v(577.63, -37.02) * mm});
            skArc(sketch, "E294", {"start": v(577.63, -37.02) * mm, "mid": v(579.75, -36.14) * mm, "end": v(580.63, -34.02) * mm});
            skArc(sketch, "E295", {"start": v(580.63, -34.02) * mm, "mid": v(579.75, -31.9) * mm, "end": v(577.63, -31.02) * mm});
            skArc(sketch, "E296", {"start": v(593.48, -507.7) * mm, "mid": v(591.36, -508.57) * mm, "end": v(590.48, -510.7) * mm});
            skArc(sketch, "E297", {"start": v(590.48, -510.7) * mm, "mid": v(591.36, -512.81) * mm, "end": v(593.48, -513.7) * mm});
            skArc(sketch, "E298", {"start": v(593.48, -513.7) * mm, "mid": v(595.6, -512.81) * mm, "end": v(596.48, -510.7) * mm});
            skArc(sketch, "E299", {"start": v(596.48, -510.7) * mm, "mid": v(595.6, -508.57) * mm, "end": v(593.48, -507.7) * mm});
            skSolve(sketch);
        }
        {
            var Q0;
            Q0=makeQuery(id+"F0.imprint","IMPRINT",FACE,{"disambiguationData":[TD([[makeQuery(id+"F0.imprint","IMPRINT",EDGE,{"derivedFrom":sQuery(id+"F0.wireOp",EDGE,"E4")}),1.0]])]});
            extrude(context, id + "F1", {"entities" : qUnion([Q0]), "depth" : 18 * mm});
        }
        {
            var Q0;
            Q0=makeQuery(id+"F0.imprint","IMPRINT",FACE,{"disambiguationData":[TD([[makeQuery(id+"F0.imprint","IMPRINT",EDGE,{"derivedFrom":sQuery(id+"F0.wireOp",EDGE,"E26")}),1.0]])]});
            extrude(context, id + "F2", {"entities" : qUnion([Q0]), "depth" : 18 * mm});
        }
        {
            var Q0;
            Q0=makeQuery(id+"F0.imprint","IMPRINT",FACE,{"disambiguationData":[TD([[makeQuery(id+"F0.imprint","IMPRINT",EDGE,{"derivedFrom":sQuery(id+"F0.wireOp",EDGE,"E104")}),1.0]])]});
            extrude(context, id + "F3", {"entities" : qUnion([Q0]), "depth" : 18 * mm});
        }
        {
            var Q0;
            Q0=makeQuery(id+"F0.imprint","IMPRINT",FACE,{"disambiguationData":[TD([[makeQuery(id+"F0.imprint","IMPRINT",EDGE,{"derivedFrom":sQuery(id+"F0.wireOp",EDGE,"E132")}),1.0]])]});
            extrude(context, id + "F4", {"entities" : qUnion([Q0]), "depth" : 18 * mm});
        }
    });
